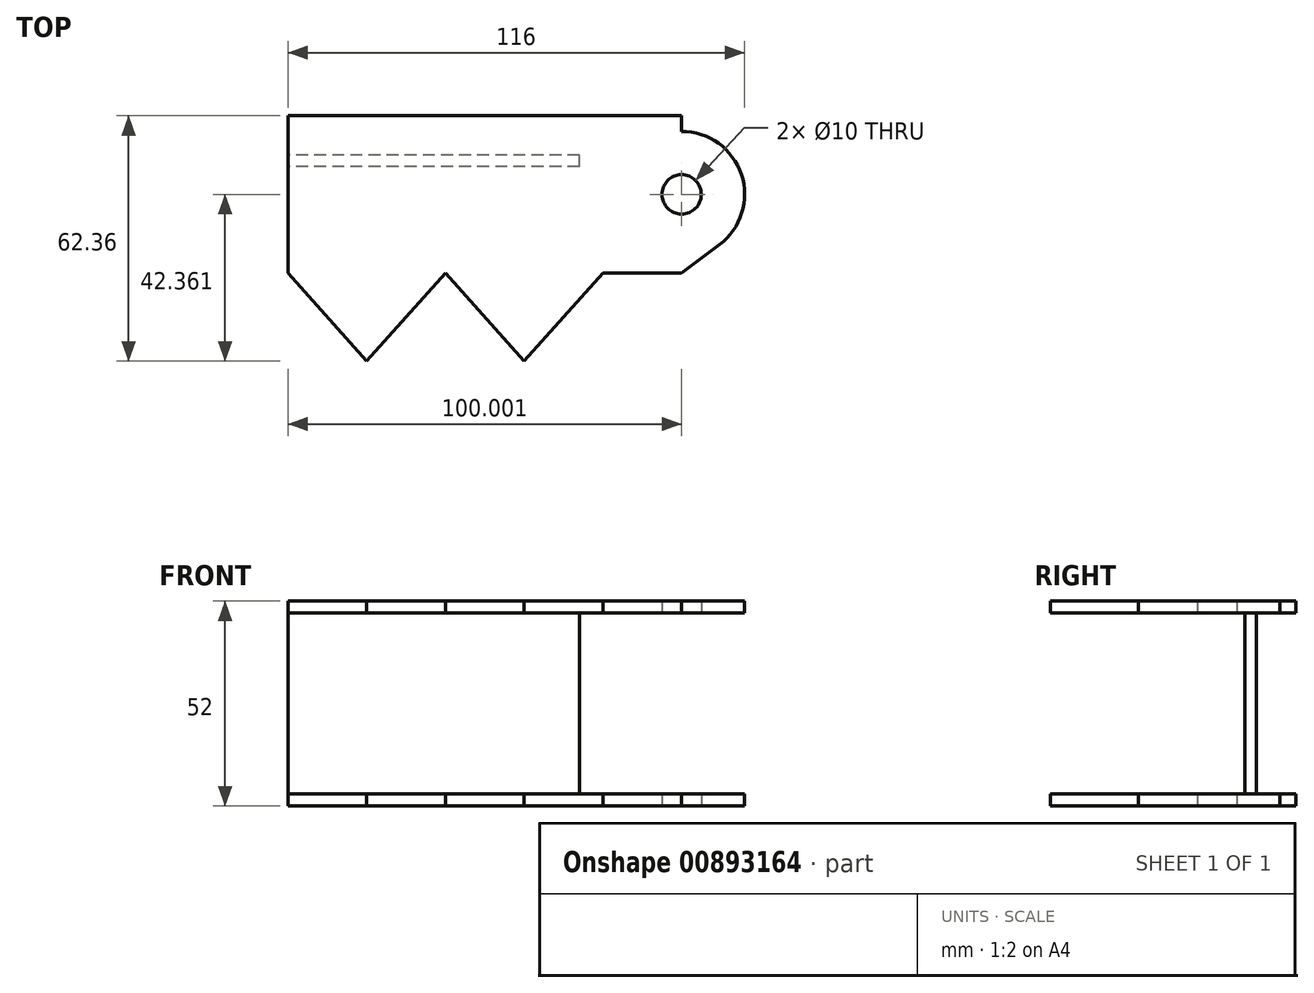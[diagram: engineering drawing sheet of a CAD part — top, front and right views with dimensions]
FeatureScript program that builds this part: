
annotation { "Feature Type Name" : "Feature", "Feature Type Description" : "" }
export const myFeature = defineFeature(function(context is Context, id is Id, definition is map)
    precondition{}
    {
        {
            var Q0;
            Q0=qCreatedBy(makeId("Top.planeOp"),FACE);
            var sketch = newSketch(context, id + "F0", { "sketchPlane" : qUnion([Q0])});
            skLineSegment(sketch, "E0", {"start": v(15.06, 37.65) * mm, "end": v(-84.94, 37.65) * mm});
            skLineSegment(sketch, "E1", {"start": v(-84.94, 37.65) * mm, "end": v(-84.94, -2.35) * mm});
            skPoint(sketch, "E2.startSnap0", {"position": v(35.06, 17.65) * mm});
            skCircle(sketch, "E3", {"center": v(15.06, 17.65) * mm, "radius": 5 * mm});
            skPoint(sketch, "E4.orphan", {"position": v(35.06, 37.65) * mm});
            skPoint(sketch, "E5.start.orphan", {"position": v(35.06, -2.35) * mm});
            skLineSegment(sketch, "E6", {"start": v(-24.94, -24.7) * mm, "end": v(-24.94, -26.77) * mm});
            skLineSegment(sketch, "E7", {"start": v(-44.94, -2.35) * mm, "end": v(-64.94, -24.7) * mm});
            skLineSegment(sketch, "E8", {"start": v(-64.94, -24.7) * mm, "end": v(-84.94, -2.35) * mm});
            skLineSegment(sketch, "E9", {"start": v(-44.94, -2.35) * mm, "end": v(-24.94, -24.7) * mm});
            skPoint(sketch, "E9.endSnap0", {"position": v(-24.94, -26.77) * mm});
            skLineSegment(sketch, "E10", {"start": v(-24.94, -24.7) * mm, "end": v(-4.94, -2.35) * mm});
            skPoint(sketch, "E11.orphan", {"position": v(-24.94, -51.18) * mm});
            skLineSegment(sketch, "E12.trimOffspring", {"start": v(-4.94, -2.35) * mm, "end": v(15.06, -2.35) * mm});
            skPoint(sketch, "E13.orphan", {"position": v(-24.94, -2.35) * mm});
            skArc(sketch, "E14", {"start": v(24.66, 4.85) * mm, "mid": v(30.24, 22.71) * mm, "end": v(15.06, 33.65) * mm});
            skLineSegment(sketch, "E15", {"start": v(15.06, 37.65) * mm, "end": v(15.06, 33.65) * mm});
            skLineSegment(sketch, "E16", {"start": v(15.06, -2.35) * mm, "end": v(24.66, 4.85) * mm});
            skSolve(sketch);
        }
        {
            var Q0;
            Q0 = qSketchRegion(id + "F0", true);
            extrude(context, id + "F1", {"entities" : qUnion([Q0]), "depth" : 52 * mm, "offsetDistance" : 25 * mm});
        }
        {
            var Q0;
            Q0=makeQuery(id+"F1.opExtrude","SWEPT_FACE",FACE,{"disambiguationData":[OSD([sQuery(id+"F0.wireOp",EDGE,"E1")])]});
            var sketch = newSketch(context, id + "F2", { "sketchPlane" : qUnion([Q0])});
            skPoint(sketch, "E17.end.orphan", {"position": v(-21.65, 52) * mm});
            skLineSegment(sketch, "E18", {"start": v(-24.65, 49) * mm, "end": v(33.97, 49) * mm});
            skLineSegment(sketch, "E19", {"start": v(33.97, 49) * mm, "end": v(33.97, 3) * mm});
            skLineSegment(sketch, "E20", {"start": v(-24.65, 49) * mm, "end": v(-24.65, 3) * mm});
            skLineSegment(sketch, "E21", {"start": v(33.97, 3) * mm, "end": v(-24.65, 3) * mm});
            skLineSegment(sketch, "E22", {"start": v(-27.65, 49) * mm, "end": v(-27.65, 3) * mm});
            skLineSegment(sketch, "E23", {"start": v(-27.65, 3) * mm, "end": v(-46, 3) * mm});
            skLineSegment(sketch, "E24", {"start": v(-46, 3) * mm, "end": v(-46, 49) * mm});
            skLineSegment(sketch, "E25", {"start": v(-46, 49) * mm, "end": v(-27.65, 49) * mm});
            skPoint(sketch, "E26.end.orphan", {"position": v(-27.65, 52) * mm});
            skSolve(sketch);
        }
        {
            var Q0;
            {var subQ0=sQuery(id+"F2.wireOp",EDGE,"E19");Q0=makeQuery(id+"F2.imprint","IMPRINT",FACE,{"disambiguationData":[TD([[makeQuery(id+"F2.imprint","IMPRINT",EDGE,{"derivedFrom":subQ0}),-1.0]])]});}
            var Q1;
            {var subQ0=sQuery(id+"F2.wireOp",EDGE,"E20");Q1=makeQuery(id+"F2.imprint","IMPRINT",FACE,{"disambiguationData":[TD([[makeQuery(id+"F2.imprint","IMPRINT",EDGE,{"derivedFrom":subQ0}),1.0]])]});}
            var Q2;
            {var subQ0=sQuery(id+"F2.wireOp",EDGE,"E24");Q2=makeQuery(id+"F2.imprint","IMPRINT",FACE,{"disambiguationData":[TD([[makeQuery(id+"F2.imprint","IMPRINT",EDGE,{"derivedFrom":subQ0}),-1.0]])]});}
            var Q3;
            {var subQ0=sQuery(id+"F2.wireOp",EDGE,"E22");Q3=makeQuery(id+"F2.imprint","IMPRINT",FACE,{"disambiguationData":[TD([[makeQuery(id+"F2.imprint","IMPRINT",EDGE,{"derivedFrom":subQ0}),-1.0]])]});}
            extrude(context, id + "F3", {"entities" : qUnion([Q0, Q1, Q2, Q3]), "operationType" : NewBodyOperationType.REMOVE, "endBound" : BoundingType.THROUGH_ALL, "oppositeDirection" : true, "depth" : 25 * mm, "offsetDistance" : 25 * mm});
        }
        {
            var Q0;
            Q0=makeQuery(id+"F3.boolean.opBoolean","INTERSECT",EDGE,{"derivedFrom":[makeQuery(id+"F1.opExtrude","SWEPT_FACE",FACE,{"disambiguationData":[OSD([sQuery(id+"F0.wireOp",EDGE,"E14")])]}),makeQuery(id+"F3.opExtrude","SWEPT_FACE",FACE,{"disambiguationData":[OSD([sQuery(id+"F2.wireOp",EDGE,"E22")])]})]});
            var Q1;
            Q1=makeQuery(id+"F3.boolean.opBoolean","COPY",EDGE,{"derivedFrom":makeQuery(id+"F3.opExtrude","CAP_EDGE",EDGE,{"disambiguationData":[OSD([sQuery(id+"F2.wireOp",EDGE,"E22")])],"isStart":true})});
            fillet(context, id + "F4", {"entities" : qUnion([Q0, Q1]), "tangentPropagation" : true, "radius" : 3 * mm, "defaultsChanged" : true, "vertexSettings" : [], "allowEdgeOverflow" : false});
        }
        {
            var Q0;
            Q0=makeQuery(id+"F3.boolean.opBoolean","COPY",FACE,{"derivedFrom":makeQuery(id+"F3.opExtrude","SWEPT_FACE",FACE,{"disambiguationData":[OSD([sQuery(id+"F2.wireOp",EDGE,"E22")])]})});
            var sketch = newSketch(context, id + "F5", { "sketchPlane" : qUnion([Q0])});
            skLineSegment(sketch, "E27", {"start": v(-39.14, 49) * mm, "end": v(-39.14, 3) * mm});
            skPoint(sketch, "E28.start.orphan", {"position": v(8.99, 49) * mm});
            skLineSegment(sketch, "E29", {"start": v(-39.14, 49) * mm, "end": v(10.86, 49) * mm});
            skLineSegment(sketch, "E30", {"start": v(10.86, 49) * mm, "end": v(10.86, 3) * mm});
            skLineSegment(sketch, "E31", {"start": v(10.86, 3) * mm, "end": v(-39.14, 3) * mm});
            skSolve(sketch);
        }
        {
            var Q0;
            Q0 = qSketchRegion(id + "F5", true);
            extrude(context, id + "F6", {"entities" : qUnion([Q0]), "operationType" : NewBodyOperationType.REMOVE, "endBound" : BoundingType.THROUGH_ALL, "oppositeDirection" : true, "depth" : 25 * mm, "offsetDistance" : 25 * mm});
        }
    });
